# Revit family: ENCBMTYP002
name_source: partatom
category: Furniture
units: mm (PartAtom-declared; Revit-internal decimal feet)

## family parameters
Always vertical = Yes
Cut with Voids When Loaded = No
OmniClass Number = 23.40.20.00
OmniClass Title = General Furniture and Specialties
Render Appearance Source = Family Geometry
Room Calculation Point = No
Shared = No
Work Plane-Based = No

## types (1)
- ENCBMTYP002
    Cost = 67647 $
    Default Elevation = 0 mm  [stored 0 ft]
    Description = 3 x Black DUPLEX OUTLET LINE 1 - 8W 4C - W/SCREW, 3 x Black DUPLEX OUTLET LINE 2 - 8W 4C - W/SCREW, 3 x Black DUPLEX OUTLET LINE 3 - 8W 4C - W/SCREW, 3 x Black DUPLEX OUTLET LINE 4 - 8W 4C - W/SCREW, 2 x 57" ELECTRICAL JUMPER  (PT 36E & VT 48), 1 x BASE INFEED - AO2/MWALL - 8 WIRE 4 CIRCUIT - SIDE MOUNTED, 3 x Slimline Scrn,Uni Spine,FVWL,Dim A,SpnMntUni,20hx36w, 3 x Slimline Scrn,Uni Spine,FVWL,Dim A,SpnMntUni,20hx42w, 6 x PEDESTAL LSERIES BOX/FILE MOBILE 24" WITH CUSHION, 3 x D2D HA 3Leg Tbl,Main Right 24x72,Return Left 30x66,2mm Edge, 3 x D2D HA 3Leg Tbl,Main Left 24x72,Return Right 30x66,2mm Edge, 2 x Encounter PwrBeam Double Sided Powered Spine Kit 78, 1 x Encounter PwrBeam Single Sided Power Spine Kit 78, 2 x Encounter PwrBeam Raceway Endcap Painted, 4 x Encounter PwrBeam 18 inch T-Leg for 29h, 1 x Encounter PwrBeam UnderMnt pole for 29h, 6 x Slimline Scrn,PM,FVWL,Dim G,UMnt,Uni,26hx66w
    Exported From CET Designer = Yes
    Manufacturer = AIS
    Model = E-MW8W4DO1
    Show ENCBMTYP002 = Yes
    VisibilityIndex = 0

note: [stored X ft] marks values corroborated as IEEE doubles in the binary element streams (Revit-internal decimal feet)

## geometry (parser evidence)
native form markers: Sweep x3
no freeform markers — native parametric forms only
